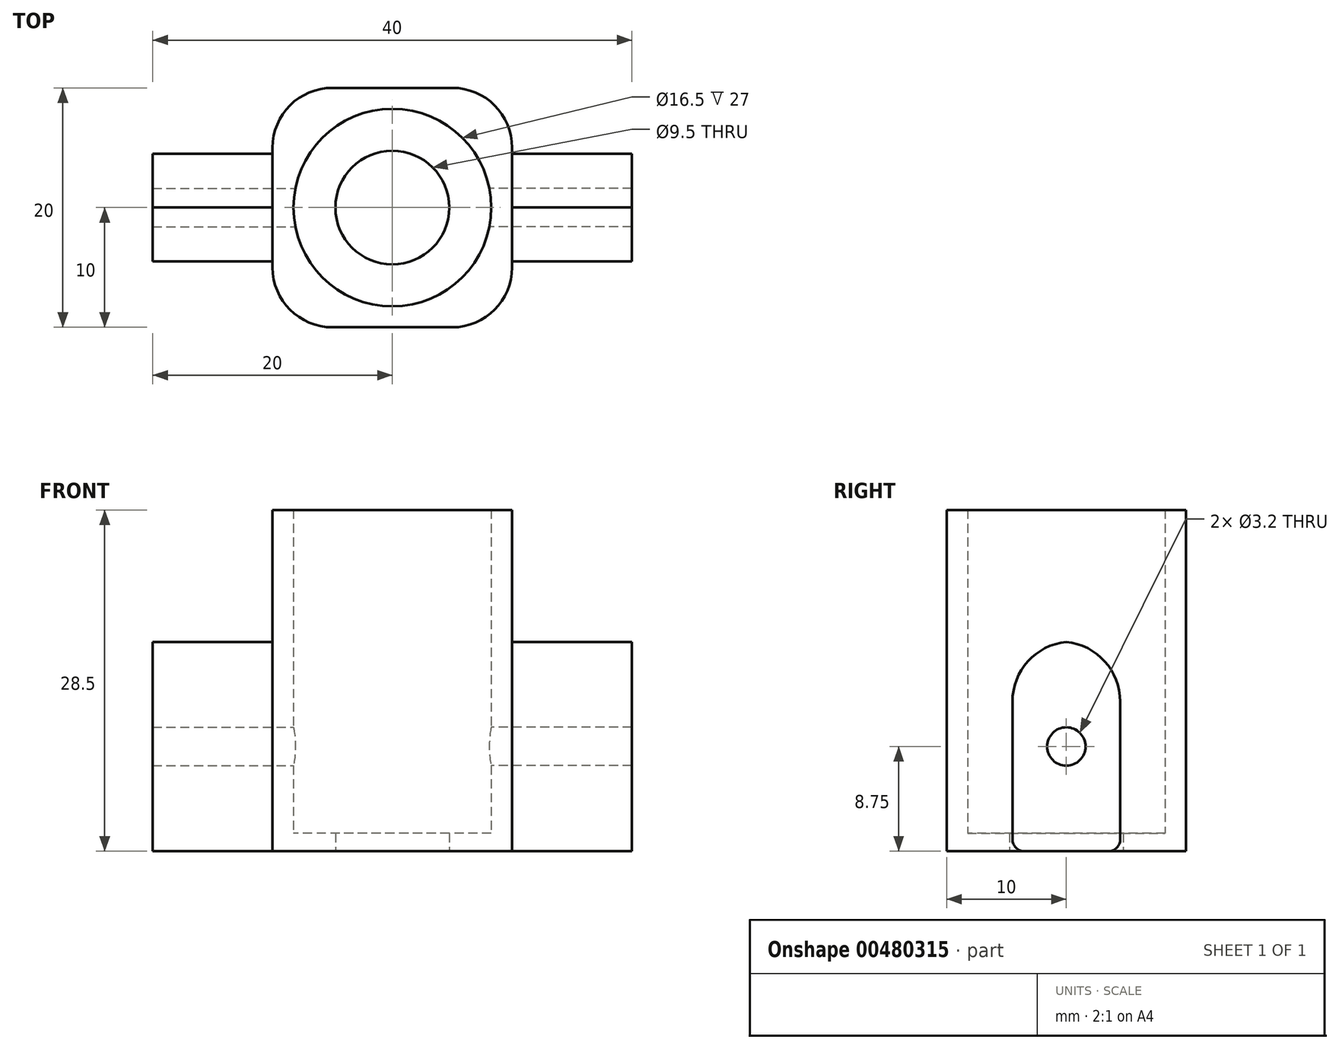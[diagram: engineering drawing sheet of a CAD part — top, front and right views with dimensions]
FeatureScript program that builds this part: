
annotation { "Feature Type Name" : "Feature", "Feature Type Description" : "" }
export const myFeature = defineFeature(function(context is Context, id is Id, definition is map)
    precondition{}
    {
        {
            var Q0;
            Q0=qCreatedBy(makeId("Top.planeOp"),FACE);
            var sketch = newSketch(context, id + "F0", { "sketchPlane" : qUnion([Q0])});
            skCircle(sketch, "E0.0", {"center": v(0, 0) * mm, "radius": 8.25 * mm});
            skCircle(sketch, "E1", {"center": v(0, 0) * mm, "radius": 4.75 * mm});
            skLineSegment(sketch, "E2.bottom", {"start": v(10, 10) * mm, "end": v(-10, 10) * mm});
            skLineSegment(sketch, "E2.top", {"start": v(10, -10) * mm, "end": v(-10, -10) * mm});
            skLineSegment(sketch, "E2.left", {"start": v(10, 10) * mm, "end": v(10, -10) * mm});
            skLineSegment(sketch, "E2.right", {"start": v(-10, 10) * mm, "end": v(-10, -10) * mm});
            skSolve(sketch);
        }
        {
            var Q0;
            Q0=makeQuery(id+"F0.imprint","IMPRINT",FACE,{"disambiguationData":[TD([[makeQuery(id+"F0.imprint","IMPRINT",EDGE,{"derivedFrom":sQuery(id+"F0.wireOp",EDGE,"E0.0")}),-1.0]])]});
            extrude(context, id + "F1", {"entities" : qUnion([Q0]), "depth" : 28.5 * mm});
        }
        {
            var Q0;
            Q0=makeQuery(id+"F0.imprint","IMPRINT",FACE,{"disambiguationData":[TD([[makeQuery(id+"F0.imprint","IMPRINT",EDGE,{"derivedFrom":sQuery(id+"F0.wireOp",EDGE,"E0.0")}),1.0]])]});
            extrude(context, id + "F2", {"entities" : qUnion([Q0]), "operationType" : NewBodyOperationType.ADD, "depth" : 1.5 * mm});
        }
        {
            var Q0;
            Q0=makeQuery(id+"F1.opExtrude","SWEPT_FACE",FACE,{"disambiguationData":[OSD([sQuery(id+"F0.wireOp",EDGE,"E2.right")])]});
            var sketch = newSketch(context, id + "F3", { "sketchPlane" : qUnion([Q0])});
            skLineSegment(sketch, "E3.bottom", {"start": v(4.5, 17.5) * mm, "end": v(-4.5, 17.5) * mm});
            skLineSegment(sketch, "E3.top", {"start": v(4.5, 0) * mm, "end": v(-4.5, 0) * mm});
            skLineSegment(sketch, "E3.left", {"start": v(4.5, 17.5) * mm, "end": v(4.5, 0) * mm});
            skLineSegment(sketch, "E3.right", {"start": v(-4.5, 17.5) * mm, "end": v(-4.5, 0) * mm});
            skPoint(sketch, "E3.middle", {"position": v(0, 8.75) * mm});
            skCircle(sketch, "E4", {"center": v(0, 8.75) * mm, "radius": 1.6 * mm});
            skSolve(sketch);
        }
        {
            var Q0;
            Q0=makeQuery(id+"F3.imprint","IMPRINT",FACE,{"disambiguationData":[TD([[makeQuery(id+"F3.imprint","IMPRINT",EDGE,{"derivedFrom":sQuery(id+"F3.wireOp",EDGE,"E3.bottom")}),1.0]])]});
            extrude(context, id + "F4", {"entities" : qUnion([Q0]), "operationType" : NewBodyOperationType.ADD, "depth" : 10 * mm});
        }
        {
            var Q0;
            Q0=makeQuery(id+"F1.opExtrude","SWEPT_FACE",FACE,{"disambiguationData":[OSD([sQuery(id+"F0.wireOp",EDGE,"E2.left")])]});
            var sketch = newSketch(context, id + "F5", { "sketchPlane" : qUnion([Q0])});
            skLineSegment(sketch, "E5.bottom", {"start": v(4.5, 0) * mm, "end": v(-4.5, 0) * mm});
            skLineSegment(sketch, "E5.top", {"start": v(4.5, 17.5) * mm, "end": v(-4.5, 17.5) * mm});
            skLineSegment(sketch, "E5.left", {"start": v(4.5, 0) * mm, "end": v(4.5, 17.5) * mm});
            skLineSegment(sketch, "E5.right", {"start": v(-4.5, 0) * mm, "end": v(-4.5, 17.5) * mm});
            skPoint(sketch, "E5.middle", {"position": v(0, 8.75) * mm});
            skSolve(sketch);
        }
        {
            var Q0;
            Q0=makeQuery(id+"F5.imprint","IMPRINT",FACE,{"disambiguationData":[TD([[makeQuery(id+"F5.imprint","IMPRINT",EDGE,{"derivedFrom":sQuery(id+"F5.wireOp",EDGE,"E5.bottom")}),-1.0]])]});
            extrude(context, id + "F6", {"entities" : qUnion([Q0]), "operationType" : NewBodyOperationType.ADD, "depth" : 10 * mm});
        }
        {
            var Q0;
            Q0=makeQuery(id+"F3.imprint","IMPRINT",FACE,{"disambiguationData":[TD([[makeQuery(id+"F3.imprint","IMPRINT",EDGE,{"derivedFrom":sQuery(id+"F3.wireOp",EDGE,"E4")}),1.0]])]});
            extrude(context, id + "F7", {"entities" : qUnion([Q0]), "operationType" : NewBodyOperationType.REMOVE, "endBound" : BoundingType.THROUGH_ALL, "oppositeDirection" : true, "depth" : 25 * mm});
        }
        {
            var Q0;
            Q0=makeQuery(id+"F1.opExtrude","SWEPT_EDGE",EDGE,{"disambiguationData":[OSD([sQuery(id+"F0.wireOp",EDGE,"E2.top"),sQuery(id+"F0.wireOp",EDGE,"E2.right")])]});
            var Q1;
            Q1=makeQuery(id+"F1.opExtrude","SWEPT_EDGE",EDGE,{"disambiguationData":[OSD([sQuery(id+"F0.wireOp",EDGE,"E2.top"),sQuery(id+"F0.wireOp",EDGE,"E2.left")])]});
            var Q2;
            Q2=makeQuery(id+"F1.opExtrude","SWEPT_EDGE",EDGE,{"disambiguationData":[OSD([sQuery(id+"F0.wireOp",EDGE,"E2.bottom"),sQuery(id+"F0.wireOp",EDGE,"E2.left")])]});
            var Q3;
            Q3=makeQuery(id+"F1.opExtrude","SWEPT_EDGE",EDGE,{"disambiguationData":[OSD([sQuery(id+"F0.wireOp",EDGE,"E2.bottom"),sQuery(id+"F0.wireOp",EDGE,"E2.right")])]});
            fillet(context, id + "F8", {"entities" : qUnion([Q0, Q1, Q2, Q3]), "radius" : 5 * mm, "tangentPropagation" : true, "allowEdgeOverflow" : false});
        }
        {
            var Q0;
            Q0=makeQuery(id+"F6.opExtrude","SWEPT_EDGE",EDGE,{"disambiguationData":[OSD([sQuery(id+"F5.wireOp",EDGE,"E5.top"),sQuery(id+"F5.wireOp",EDGE,"E5.right")])]});
            var Q1;
            Q1=makeQuery(id+"F6.opExtrude","SWEPT_EDGE",EDGE,{"disambiguationData":[OSD([sQuery(id+"F5.wireOp",EDGE,"E5.top"),sQuery(id+"F5.wireOp",EDGE,"E5.left")])]});
            fillet(context, id + "F9", {"entities" : qUnion([Q0, Q1]), "radius" : 5 * mm, "tangentPropagation" : true, "allowEdgeOverflow" : false});
        }
        {
            var Q0;
            Q0=makeQuery(id+"F4.opExtrude","SWEPT_EDGE",EDGE,{"disambiguationData":[OSD([sQuery(id+"F3.wireOp",EDGE,"E3.bottom"),sQuery(id+"F3.wireOp",EDGE,"E3.left")])]});
            var Q1;
            Q1=makeQuery(id+"F4.opExtrude","SWEPT_EDGE",EDGE,{"disambiguationData":[OSD([sQuery(id+"F3.wireOp",EDGE,"E3.bottom"),sQuery(id+"F3.wireOp",EDGE,"E3.right")])]});
            fillet(context, id + "F10", {"entities" : qUnion([Q0, Q1]), "radius" : 5 * mm, "tangentPropagation" : true, "allowEdgeOverflow" : false});
        }
        {
            var Q0;
            Q0=makeQuery(id+"F6.opExtrude","SWEPT_EDGE",EDGE,{"disambiguationData":[OSD([sQuery(id+"F0.wireOp",EDGE,"E2.left"),sQuery(id+"F5.wireOp",EDGE,"E5.bottom"),sQuery(id+"F5.wireOp",EDGE,"E5.right")])]});
            var Q1;
            Q1=makeQuery(id+"F6.opExtrude","SWEPT_EDGE",EDGE,{"disambiguationData":[OSD([sQuery(id+"F0.wireOp",EDGE,"E2.left"),sQuery(id+"F5.wireOp",EDGE,"E5.bottom"),sQuery(id+"F5.wireOp",EDGE,"E5.left")])]});
            var Q2;
            Q2=makeQuery(id+"F4.opExtrude","SWEPT_EDGE",EDGE,{"disambiguationData":[OSD([sQuery(id+"F0.wireOp",EDGE,"E2.right"),sQuery(id+"F3.wireOp",EDGE,"E3.top"),sQuery(id+"F3.wireOp",EDGE,"E3.right")])]});
            var Q3;
            Q3=makeQuery(id+"F4.opExtrude","SWEPT_EDGE",EDGE,{"disambiguationData":[OSD([sQuery(id+"F0.wireOp",EDGE,"E2.right"),sQuery(id+"F3.wireOp",EDGE,"E3.top"),sQuery(id+"F3.wireOp",EDGE,"E3.left")])]});
            fillet(context, id + "F11", {"entities" : qUnion([Q0, Q1, Q2, Q3]), "radius" : 1 * mm, "tangentPropagation" : true, "allowEdgeOverflow" : false});
        }
    });
